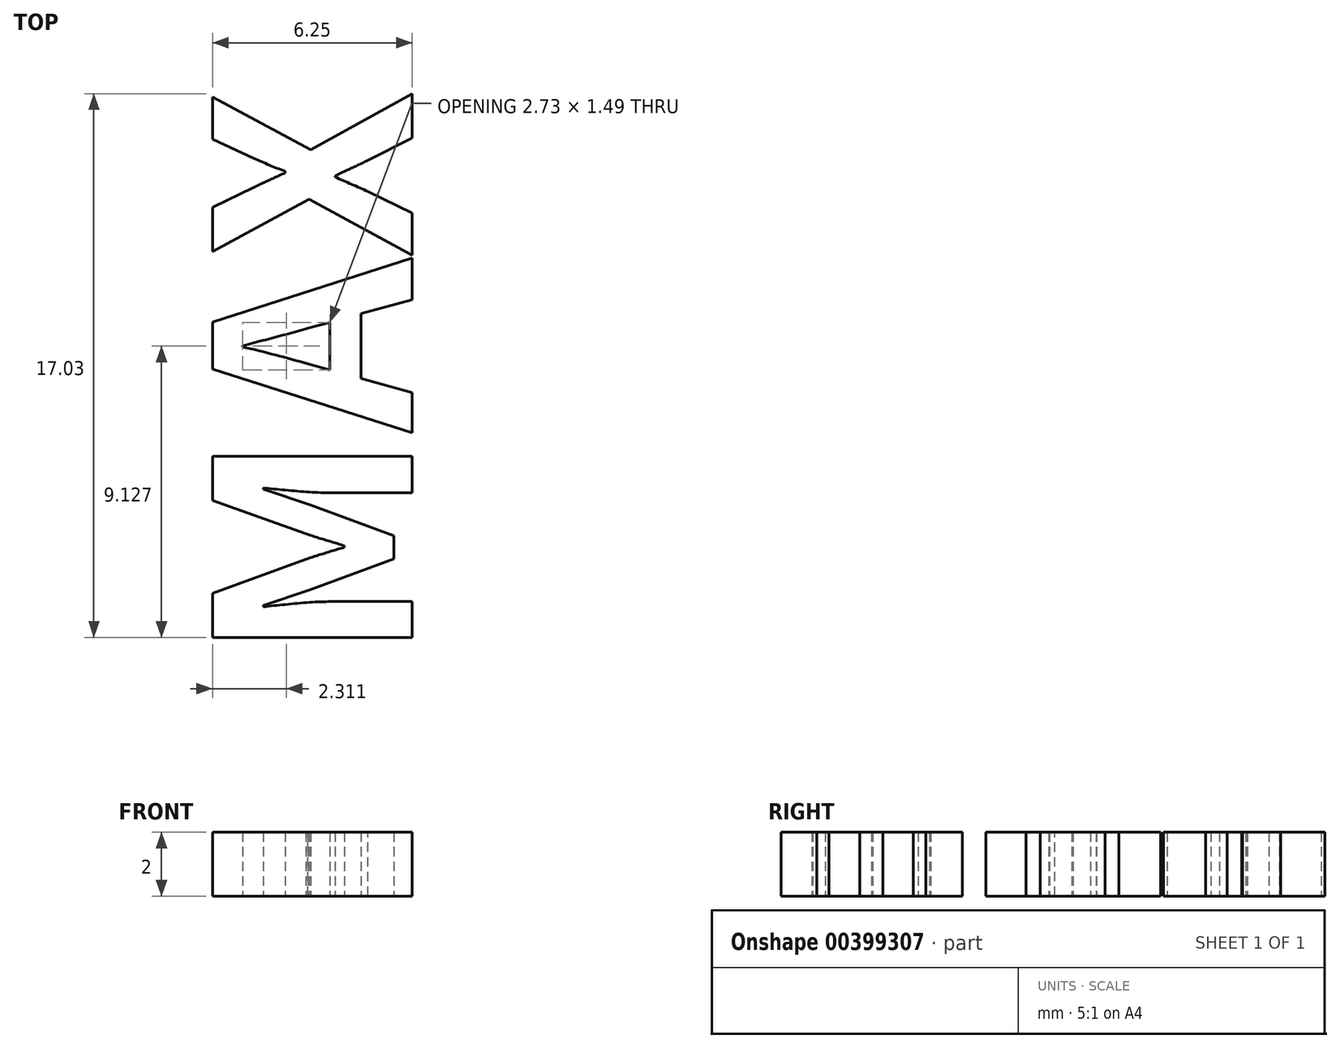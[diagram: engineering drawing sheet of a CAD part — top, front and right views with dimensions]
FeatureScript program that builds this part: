
annotation { "Feature Type Name" : "Feature", "Feature Type Description" : "" }
export const myFeature = defineFeature(function(context is Context, id is Id, definition is map)
    precondition{}
    {
        {
            var Q0;
            Q0=qCreatedBy(makeId("Top.planeOp"),FACE);
            var sketch = newSketch(context, id + "F0", { "sketchPlane" : qUnion([Q0])});
            skText(sketch, "E0", { "text": "MAX", "fontName": "NotoSansCJKkr-Bold.otf"});
            const initialGuessF0  = {"E0": [0.03933, -0.01552, 0, 1, 0.00608]};
            skSetInitialGuess(sketch, initialGuessF0);
            skSolve(sketch);
        }
        {
            var Q0;
            Q0 = qSketchRegion(id + "F0", true);
            extrude(context, id + "F1", {"entities" : qUnion([Q0]), "depth" : 2 * mm, "offsetDistance" : 25 * mm});
        }
    });
